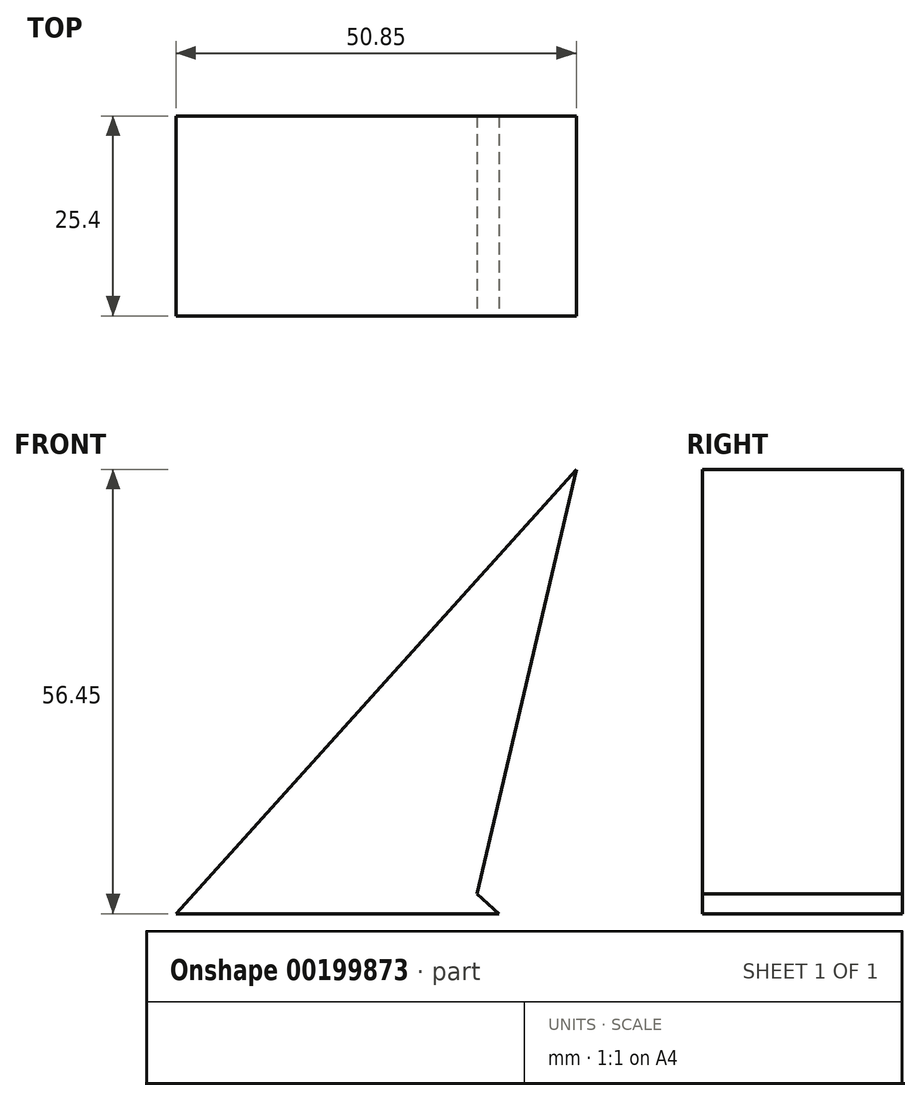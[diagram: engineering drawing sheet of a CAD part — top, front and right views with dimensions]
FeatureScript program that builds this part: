
annotation { "Feature Type Name" : "Feature", "Feature Type Description" : "" }
export const myFeature = defineFeature(function(context is Context, id is Id, definition is map)
    precondition{}
    {
        {
            var Q0;
            Q0=qCreatedBy(makeId("Front.planeOp"),FACE);
            var sketch = newSketch(context, id + "F0", { "sketchPlane" : qUnion([Q0])});
            skLineSegment(sketch, "E0", {"start": v(41.03, 0) * mm, "end": v(0, 0) * mm});
            skLineSegment(sketch, "E1", {"start": v(0, 0) * mm, "end": v(50.85, 56.45) * mm});
            skLineSegment(sketch, "E2", {"start": v(50.85, 56.45) * mm, "end": v(50.85, 56.45) * mm});
            skLineSegment(sketch, "E3", {"start": v(38.22, 2.48) * mm, "end": v(41.03, 0) * mm});
            skLineSegment(sketch, "E4", {"start": v(50.85, 56.45) * mm, "end": v(38.22, 2.48) * mm});
            skSolve(sketch);
        }
        {
            var Q0;
            Q0=makeQuery(id+"F0.imprint","IMPRINT",FACE,{"disambiguationData":[TD([[makeQuery(id+"F0.imprint","IMPRINT",EDGE,{"derivedFrom":sQuery(id+"F0.wireOp",EDGE,"E0")}),-1.0]])]});
            extrude(context, id + "F1", {"entities" : qUnion([Q0]), "oppositeDirection" : true, "depth" : 25.4 * mm});
        }
    });
